# Revit family: Holyoake_-_PRD_Pressure Relief Damper Channel Frame
name_source: partatom
category: Duct Accessories
revit_build: Autodesk Revit 2014 (Build: 20130308_1515(x64)
units: mm (PartAtom-declared; Revit-internal decimal feet)

## types (1)
- Holyoake_-_PRD_Pressure Relief Damper Channel Frame
    Blade Angle = 65.00°
    Channel Frame H = 25 mm  [stored 0.082021 ft]
    Channel Frame W = 127 mm
    H = 625 mm  [stored 2.05052 ft]
    Manufacturer = Holyoake Industries Ltd.
    Material = Aluminium
    Maximum Height = 1544 mm  [stored 5.06562 ft]
    Maximum Width = 800 mm  [stored 2.62467 ft]
    Minimum Height = 230 mm  [stored 0.754593 ft]
    Minimum Width = 200 mm  [stored 0.656168 ft]
    Model = PRD150 Channel Frame
    Nominal H = 675 mm  [stored 2.21457 ft]
    Nominal W = 600 mm
    Parametric H = 800 mm  [stored 2.62467 ft]
    Parametric W = 600 mm
    URL = http://www.productspec.net
    W = 550 mm

note: [stored X ft] marks values corroborated as IEEE doubles in the binary element streams (Revit-internal decimal feet)

## geometry (parser evidence)
native form markers: Sweep x14
no freeform markers — native parametric forms only
